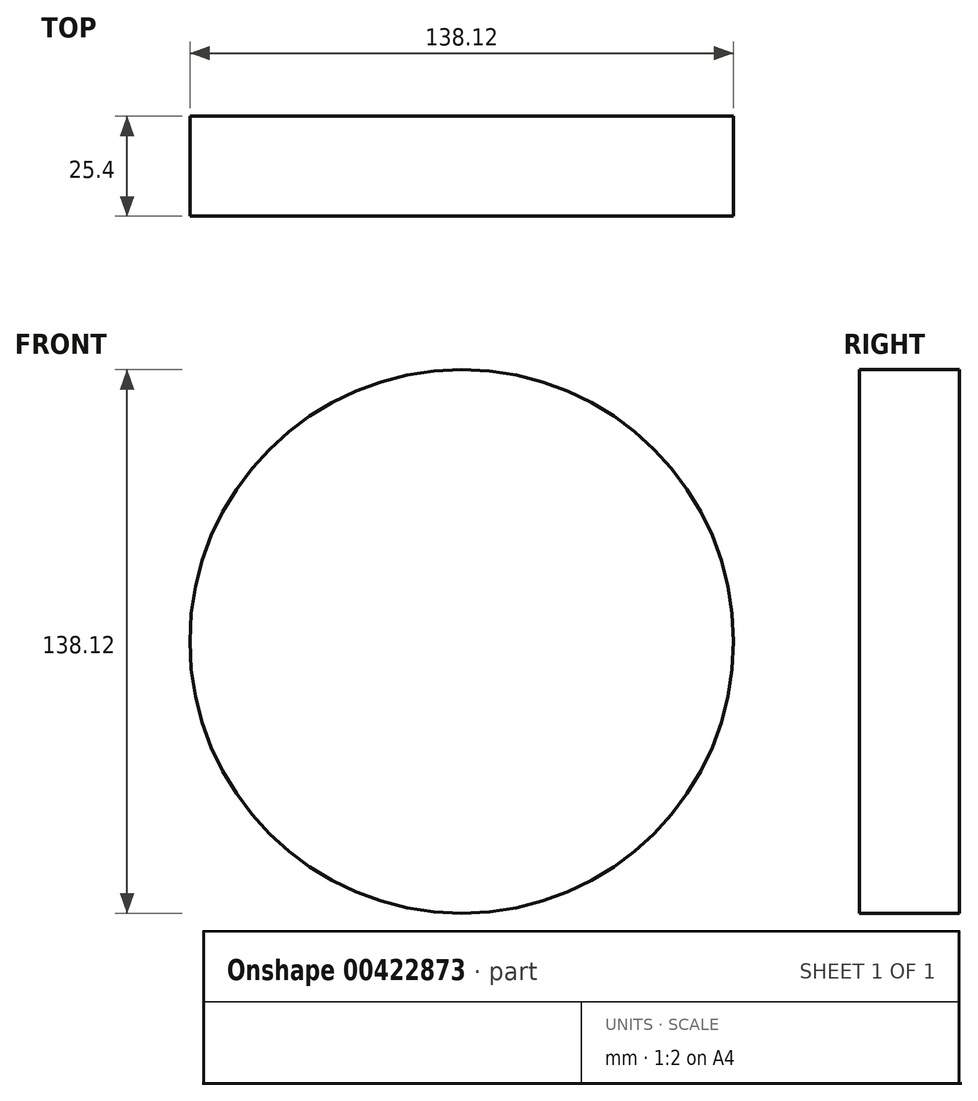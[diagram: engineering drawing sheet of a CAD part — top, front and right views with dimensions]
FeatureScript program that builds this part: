
annotation { "Feature Type Name" : "Feature", "Feature Type Description" : "" }
export const myFeature = defineFeature(function(context is Context, id is Id, definition is map)
    precondition{}
    {
        {
            var Q0;
            Q0=qCreatedBy(makeId("Front.planeOp"),FACE);
            var sketch = newSketch(context, id + "F0", { "sketchPlane" : qUnion([Q0])});
            skCircle(sketch, "E0", {"center": v(0, 0) * mm, "radius": 69.06 * mm});
            skSolve(sketch);
        }
        {
            var Q0;
            Q0=makeQuery(id+"F0.imprint","IMPRINT",FACE,{"disambiguationData":[TD([[makeQuery(id+"F0.imprint","IMPRINT",EDGE,{"derivedFrom":sQuery(id+"F0.wireOp",EDGE,"E0")}),1.0]])]});
            var Q1;
            Q1=sQuery(id+"F0.wireOp",EDGE,"E0");
            extrude(context, id + "F1", {"entities" : qUnion([Q0]), "bodyType" : ToolBodyType.SURFACE, "surfaceEntities" : qUnion([Q1]), "depth" : 25.4 * mm});
        }
    });
